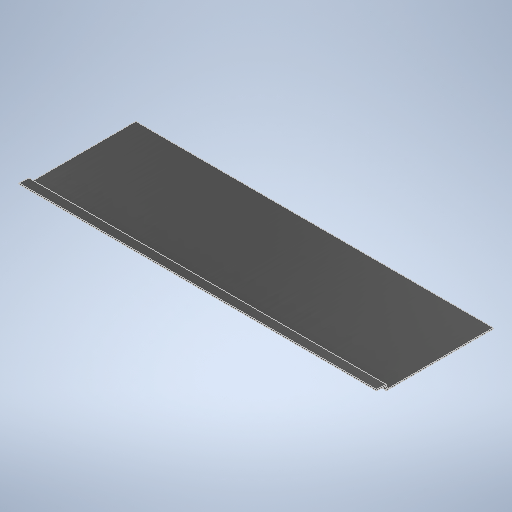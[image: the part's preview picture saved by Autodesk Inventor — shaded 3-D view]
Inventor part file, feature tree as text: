
AUTODESK INVENTOR PART (.ipt)
format: ipt  version: 2025.1 (Build 291241020, 241B)  size: 287,232 bytes
history: native  units: in
note: dims shown in document units (in); Inventor stores cm internally (conversion verified against a paired STEP export)
features: extrude x1, sketch x1
ambient origin geometry x8: Origin, YZ Plane, XZ Plane, XY Plane, X Axis, Y Axis, Z Axis, Center Point
bodies: Body1 (feature_tree)
feature tree (2):
  extrude  "Extrusion4"  Depth=0.125in
  sketch  "Sketch1"  dims[d0=23.408in d1=0.125in d2=0.265in d7=0.125in d8=0.237in d9=1.1431in d10=0.125in d11=0.7449in d12=0.125in d13=12.09in d18=0.125in d20=12.0907in d21=0.3425in d22=0.125in d23=0.125in d24=0.1549in d25=0.661in d28=0.125in d29=0.1254in d30=0.125in d32=0.125in d33=0.125in d34=5.625in d35=6.6451in d36=0.4476in d37=0.0449in d38=6.112in d41=0.125in d42=0.125in d43=0.125in d44=5.625in d45=11.655in d46=1.1103in d47=0.4636in d48=0.0215in d49=39.375in d50=0.0in d51=0.125in d52=0.125in d53=0.1035in]
